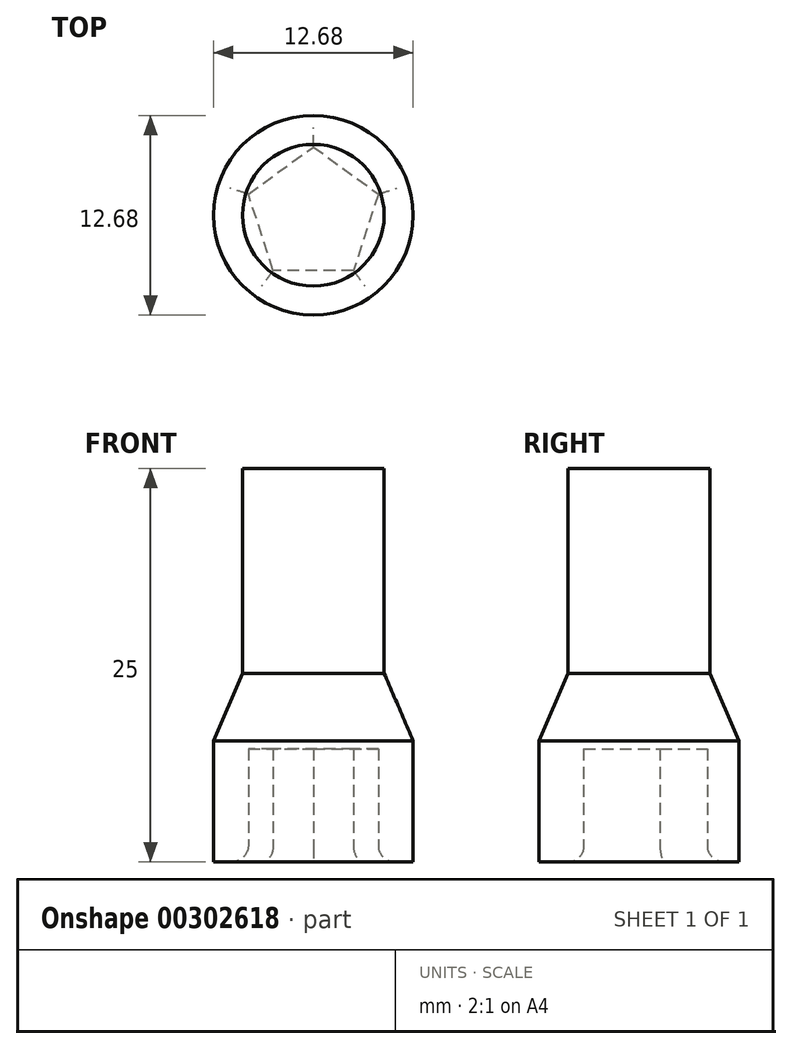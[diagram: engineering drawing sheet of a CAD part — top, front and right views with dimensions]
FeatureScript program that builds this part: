
annotation { "Feature Type Name" : "Feature", "Feature Type Description" : "" }
export const myFeature = defineFeature(function(context is Context, id is Id, definition is map)
    precondition{}
    {
        {
            var Q0;
            Q0=qCreatedBy(makeId("Top.planeOp"),FACE);
            var sketch = newSketch(context, id + "F0", { "sketchPlane" : qUnion([Q0])});
            skCircle(sketch, "E0.cCircle", {"center": v(0, 0) * mm, "radius": 3.51 * mm, "construction": true});
            skLineSegment(sketch, "E0.0", {"start": v(-4.13, 1.34) * mm, "end": v(0, 4.34) * mm});
            skLineSegment(sketch, "E0.1", {"start": v(0, 4.34) * mm, "end": v(4.13, 1.34) * mm});
            skLineSegment(sketch, "E0.2", {"start": v(4.13, 1.34) * mm, "end": v(2.55, -3.51) * mm});
            skLineSegment(sketch, "E0.3", {"start": v(2.55, -3.51) * mm, "end": v(-2.55, -3.51) * mm});
            skLineSegment(sketch, "E0.4", {"start": v(-2.55, -3.51) * mm, "end": v(-4.13, 1.34) * mm});
            skPoint(sketch, "E0.0.midPoint", {"position": v(-2.06, 2.84) * mm});
            skCircle(sketch, "E1", {"center": v(0, 0) * mm, "radius": 6.34 * mm});
            skSolve(sketch);
        }
        {
            var Q0;
            Q0=makeQuery(id+"F0.imprint","IMPRINT",FACE,{"disambiguationData":[TD([[makeQuery(id+"F0.imprint","IMPRINT",EDGE,{"derivedFrom":sQuery(id+"F0.wireOp",EDGE,"E0.0")}),1.0]])]});
            extrude(context, id + "F1", {"entities" : qUnion([Q0]), "depth" : 7.2 * mm});
        }
        {
            var Q0;
            Q0=makeQuery(id+"F1.opExtrude","CAP_FACE",FACE,{"disambiguationData":[OSD([sQuery(id+"F0.wireOp",EDGE,"E0.0"),sQuery(id+"F0.wireOp",EDGE,"E0.1"),sQuery(id+"F0.wireOp",EDGE,"E0.2"),sQuery(id+"F0.wireOp",EDGE,"E0.3"),sQuery(id+"F0.wireOp",EDGE,"E0.4"),sQuery(id+"F0.wireOp",EDGE,"E1")])],"isStart":false});
            var sketch = newSketch(context, id + "F2", { "sketchPlane" : qUnion([Q0])});
            skCircle(sketch, "E2.0", {"center": v(0, 0) * mm, "radius": 6.34 * mm});
            skPoint(sketch, "E3", {"position": v(-6.34, 0) * mm});
            skSolve(sketch);
        }
        {
            var Q0;
            Q0=makeQuery(id+"F2.imprint","IMPRINT",FACE,{"disambiguationData":[TD([[makeQuery(id+"F2.imprint","IMPRINT",EDGE,{"derivedFrom":sQuery(id+"F2.wireOp",EDGE,"E2.0")}),1.0]])]});
            var Q1;
            Q1=makeQuery(id+"F2.imprint","IMPRINT",FACE,{"disambiguationData":[TD([[makeQuery(id+"F2.imprint","IMPRINT",EDGE,{"derivedFrom":makeQuery(id+"F1.opExtrude","CAP_EDGE",EDGE,{"disambiguationData":[OSD([sQuery(id+"F0.wireOp",EDGE,"E0.0")])],"isStart":false})}),-1.0]])]});
            extrude(context, id + "F3", {"entities" : qUnion([Q0, Q1]), "operationType" : NewBodyOperationType.ADD, "depth" : .5 * mm});
        }
        {
            var Q0;
            Q0=qCreatedBy(makeId("Top.planeOp"),FACE);
            cPlane(context, id + "F4", {"entities" : qUnion([Q0]), "cplaneType" : CPlaneType.OFFSET, "offset" : 12 * mm, "width" : 150 * mm, "height" : 150 * mm});
        }
        {
            var Q0;
            Q0=qCreatedBy(id+"F4.planeOp",FACE);
            var sketch = newSketch(context, id + "F5", { "sketchPlane" : qUnion([Q0])});
            skCircle(sketch, "E4", {"center": v(0, 0) * mm, "radius": 4.5 * mm});
            skSolve(sketch);
        }
        {
            var Q1;
            Q1=makeQuery(id+"F3.opExtrude","CAP_FACE",FACE,{"disambiguationData":[OSD([sQuery(id+"F2.wireOp",EDGE,"E2.0")])],"isStart":false});
            var Q2;
            Q2=makeQuery(id+"F5.imprint","IMPRINT",FACE,{"disambiguationData":[TD([[makeQuery(id+"F5.imprint","IMPRINT",EDGE,{"derivedFrom":sQuery(id+"F5.wireOp",EDGE,"E4")}),1.0]])]});
            loft(context, id + "F6", {"operationType" : NewBodyOperationType.ADD, "sheetProfilesArray" : [{ "sheetProfileEntities" : qUnion([Q1]) }, { "sheetProfileEntities" : qUnion([Q2]) }]});
        }
        {
            var Q0;
            Q0=makeQuery(id+"F6.opLoft","CAP_FACE",FACE,{"disambiguationData":[OSD([makeQuery(id+"F5.imprint","IMPRINT",FACE,{"disambiguationData":[TD([[makeQuery(id+"F5.imprint","IMPRINT",EDGE,{"derivedFrom":sQuery(id+"F5.wireOp",EDGE,"E4")}),1.0]])]})])],"isStart":true});
            extrude(context, id + "F7", {"entities" : qUnion([Q0]), "operationType" : NewBodyOperationType.ADD, "depth" : 13 * mm});
        }
        {
            var Q0;
            Q0=makeQuery(id+"F1.opExtrude","CAP_EDGE",EDGE,{"disambiguationData":[OSD([sQuery(id+"F0.wireOp",EDGE,"E0.4")])],"isStart":true});
            var Q1;
            Q1=makeQuery(id+"F1.opExtrude","CAP_EDGE",EDGE,{"disambiguationData":[OSD([sQuery(id+"F0.wireOp",EDGE,"E0.3")])],"isStart":true});
            var Q2;
            Q2=makeQuery(id+"F1.opExtrude","CAP_EDGE",EDGE,{"disambiguationData":[OSD([sQuery(id+"F0.wireOp",EDGE,"E0.2")])],"isStart":true});
            var Q3;
            Q3=makeQuery(id+"F1.opExtrude","CAP_EDGE",EDGE,{"disambiguationData":[OSD([sQuery(id+"F0.wireOp",EDGE,"E0.1")])],"isStart":true});
            var Q4;
            Q4=makeQuery(id+"F1.opExtrude","CAP_EDGE",EDGE,{"disambiguationData":[OSD([sQuery(id+"F0.wireOp",EDGE,"E0.0")])],"isStart":true});
            fillet(context, id + "F8", {"entities" : qUnion([Q0, Q1, Q2, Q3, Q4]), "radius" : 1 * mm, "tangentPropagation" : true, "allowEdgeOverflow" : false});
        }
    });
